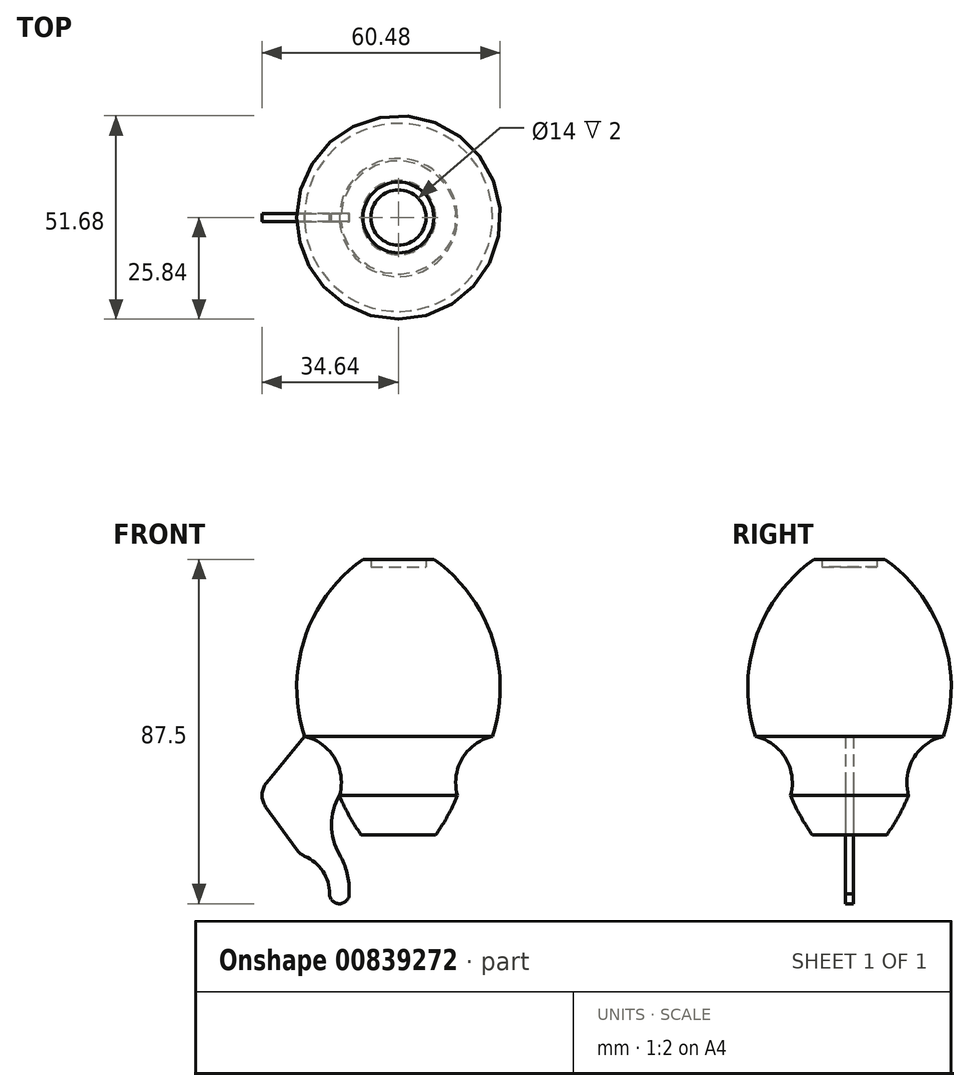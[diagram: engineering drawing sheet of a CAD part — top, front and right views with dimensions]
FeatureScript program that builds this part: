
annotation { "Feature Type Name" : "Feature", "Feature Type Description" : "" }
export const myFeature = defineFeature(function(context is Context, id is Id, definition is map)
    precondition{}
    {
        {
            var Q0;
            Q0=qCreatedBy(makeId("Front.planeOp"),FACE);
            var sketch = newSketch(context, id + "F0", { "sketchPlane" : qUnion([Q0])});
            skLineSegment(sketch, "E0", {"start": v(0, 0) * mm, "end": v(0, 80) * mm});
            skLineSegment(sketch, "E1", {"start": v(0, 80) * mm, "end": v(9, 80) * mm});
            skLineSegment(sketch, "E2", {"start": v(0, 20) * mm, "end": v(15, 20) * mm});
            skLineSegment(sketch, "E3", {"start": v(0, 35) * mm, "end": v(23.88, 35) * mm});
            skArc(sketch, "E4", {"start": v(23.88, 35) * mm, "mid": v(23.82, 59.94) * mm, "end": v(9, 80) * mm});
            skArc(sketch, "E5", {"start": v(23.88, 35) * mm, "mid": v(16.21, 29.41) * mm, "end": v(15, 20) * mm});
            skArc(sketch, "E6", {"start": v(0, 0) * mm, "mid": v(8.77, 9.05) * mm, "end": v(15, 20) * mm});
            skLineSegment(sketch, "E7", {"start": v(0, 78) * mm, "end": v(7, 78) * mm});
            skLineSegment(sketch, "E8", {"start": v(7, 78) * mm, "end": v(7, 80) * mm});
            skSolve(sketch);
        }
        {
            var Q0;
            {var subQ3=sQuery(id+"F0.wireOp",EDGE,"E3");Q0=makeQuery(id+"F0.imprint","IMPRINT",FACE,{"disambiguationData":[TD([[makeQuery(id+"F0.imprint","IMPRINT",EDGE,{"derivedFrom":subQ3}),1.0]])]});}
            var Q1;
            {var subQ0=sQuery(id+"F0.wireOp",EDGE,"E2");Q1=makeQuery(id+"F0.imprint","IMPRINT",FACE,{"disambiguationData":[TD([[makeQuery(id+"F0.imprint","IMPRINT",EDGE,{"derivedFrom":subQ0}),1.0]])]});}
            var Q2;
            {var subQ2=sQuery(id+"F0.wireOp",EDGE,"E2");Q2=makeQuery(id+"F0.imprint","IMPRINT",FACE,{"disambiguationData":[TD([[makeQuery(id+"F0.imprint","IMPRINT",EDGE,{"derivedFrom":subQ2}),-1.0]])]});}
            var Q3;
            Q3=sQuery(id+"F0.wireOp",EDGE,"E0");
            revolve(context, id + "F1", {"surfaceOperationType" : NewSurfaceOperationType.NEW, "entities" : qUnion([Q0, Q1, Q2]), "axis" : qUnion([Q3]), "revolveType" : RevolveType.FULL});
        }
        {
            var Q0;
            Q0=qCreatedBy(makeId("Front.planeOp"),FACE);
            var sketch = newSketch(context, id + "F2", { "sketchPlane" : qUnion([Q0])});
            skLineSegment(sketch, "E9.0", {"start": v(23.88, 35) * mm, "end": v(-23.88, 35) * mm});
            skLineSegment(sketch, "E10.0", {"start": v(15, 20) * mm, "end": v(-15, 20) * mm});
            skLineSegment(sketch, "E11", {"start": v(-23.88, 35) * mm, "end": v(-15, 20) * mm});
            skLineSegment(sketch, "E12", {"start": v(0, 35) * mm, "end": v(0, 20) * mm});
            skSolve(sketch);
        }
        {
            var Q0;
            Q0 = qSketchRegion(id + "F2", true);
            extrude(context, id + "F3", {"entities" : qUnion([Q0]), "operationType" : NewBodyOperationType.ADD, "endBound" : BoundingType.SYMMETRIC, "depth" : 2 * mm, "offsetDistance" : 25 * mm});
        }
        {
            var Q0;
            Q0=qCreatedBy(makeId("Front.planeOp"),FACE);
            var sketch = newSketch(context, id + "F4", { "sketchPlane" : qUnion([Q0])});
            skLineSegment(sketch, "E13", {"start": v(0, 0) * mm, "end": v(0, -5) * mm});
            skLineSegment(sketch, "E14", {"start": v(0, -5) * mm, "end": v(-15, -5) * mm});
            skLineSegment(sketch, "E15", {"start": v(-15, -5) * mm, "end": v(-15, 5) * mm});
            skLineSegment(sketch, "E16", {"start": v(-15, 5) * mm, "end": v(-25, 5) * mm});
            skArc(sketch, "E17", {"start": v(-17.5, -5) * mm, "mid": v(-15, -7.5) * mm, "end": v(-12.5, -5) * mm});
            skLineSegment(sketch, "E18", {"start": v(-15, -5) * mm, "end": v(-17.5, -5) * mm});
            skFitSpline(sketch, "E19.0", {"points": [v(-23.86, 35) * mm, v(-23.46, 34.91) * mm, v(-22.67, 34.69) * mm, v(-21.54, 34.24) * mm, v(-20.46, 33.68) * mm, v(-19.6, 33.13) * mm, v(-18.96, 32.63) * mm, v(-18.34, 32.1) * mm, v(-17.62, 31.39) * mm, v(-16.85, 30.45) * mm, v(-16.16, 29.42) * mm, v(-15.6, 28.35) * mm, v(-15.22, 27.4) * mm, v(-14.97, 26.63) * mm, v(-14.76, 25.84) * mm, v(-14.62, 25.04) * mm, v(-14.53, 24.22) * mm, v(-14.5, 23.4) * mm, v(-14.53, 21.98) * mm, v(-14.74, 20.79) * mm, v(-14.97, 20) * mm]});
            skArc(sketch, "E20", {"start": v(-14.97, 20) * mm, "mid": v(-17, 12.5) * mm, "end": v(-15, 5) * mm});
            skArc(sketch, "E21", {"start": v(-12.5, -5) * mm, "mid": v(-13.05, 0.17) * mm, "end": v(-15, 5) * mm});
            skArc(sketch, "E22", {"start": v(-17.5, -5) * mm, "mid": v(-19.22, 0.73) * mm, "end": v(-23.8, 4.57) * mm});
            skLineSegment(sketch, "E23", {"start": v(-23.86, 35) * mm, "end": v(-33.5, 23.24) * mm});
            skLineSegment(sketch, "E24", {"start": v(-33.7, 17.16) * mm, "end": v(-25.9, 6.25) * mm});
            skPoint(sketch, "E25.visualSharp", {"position": v(-35.94, 20.27) * mm});
            skArc(sketch, "E25.filletArc", {"start": v(-33.5, 23.24) * mm, "mid": v(-34.64, 20.23) * mm, "end": v(-33.7, 17.16) * mm});
            skPoint(sketch, "E26.visualSharp", {"position": v(-25, 5) * mm});
            skArc(sketch, "E26.filletArc", {"start": v(-25.9, 6.25) * mm, "mid": v(-24.97, 5.27) * mm, "end": v(-23.8, 4.57) * mm});
            skSolve(sketch);
        }
        {
            var Q0;
            Q0=makeQuery(id+"F4.imprint","IMPRINT",FACE,{"disambiguationData":[TD([[makeQuery(id+"F4.imprint","IMPRINT",EDGE,{"derivedFrom":sQuery(id+"F4.wireOp",EDGE,"E19.0")}),-1.0]])]});
            var Q1;
            {var subQ2=sQuery(id+"F4.wireOp",EDGE,"E15");Q1=makeQuery(id+"F4.imprint","IMPRINT",FACE,{"disambiguationData":[TD([[makeQuery(id+"F4.imprint","IMPRINT",EDGE,{"derivedFrom":subQ2}),1.0]])]});}
            var Q2;
            {var subQ2=sQuery(id+"F4.wireOp",EDGE,"E17");Q2=makeQuery(id+"F4.imprint","IMPRINT",FACE,{"disambiguationData":[TD([[makeQuery(id+"F4.imprint","IMPRINT",EDGE,{"derivedFrom":subQ2}),1.0]])]});}
            var Q3;
            {var subQ0=sQuery(id+"F4.wireOp",EDGE,"E15");Q3=makeQuery(id+"F4.imprint","IMPRINT",FACE,{"disambiguationData":[TD([[makeQuery(id+"F4.imprint","IMPRINT",EDGE,{"derivedFrom":subQ0}),-1.0]])]});}
            extrude(context, id + "F5", {"entities" : qUnion([Q0, Q1, Q2, Q3]), "operationType" : NewBodyOperationType.ADD, "endBound" : BoundingType.SYMMETRIC, "depth" : 2 * mm, "offsetDistance" : 25 * mm});
        }
        {
            var Q0;
            Q0=qCreatedBy(makeId("Top.planeOp"),FACE);
            var sketch = newSketch(context, id + "F6", { "sketchPlane" : qUnion([Q0])});
            skCircle(sketch, "E27", {"center": v(0, 0) * mm, "radius": 10 * mm});
            skSolve(sketch);
        }
        {
            var Q0;
            Q0 = qSketchRegion(id + "F6", true);
            extrude(context, id + "F7", {"entities" : qUnion([Q0]), "operationType" : NewBodyOperationType.REMOVE, "depth" : 10 * mm, "offsetDistance" : 25 * mm});
        }
    });
